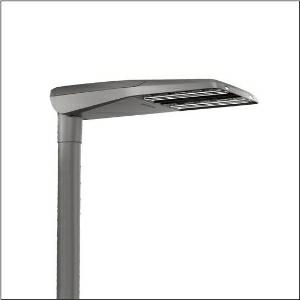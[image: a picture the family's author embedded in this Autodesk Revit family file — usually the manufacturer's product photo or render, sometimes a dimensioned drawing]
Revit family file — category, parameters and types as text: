
# Revit family: streetlight_sl_11_iq_midi___st1_0ab_5xc3n41f08le_a448
name_source: partatom
category: Lighting Fixtures
units: mm (PartAtom-declared; Revit-internal decimal feet)

## family parameters
Cut with Voids When Loaded = No
Host = Face
Light Source = No
Part Type = Normal
Room Calculation Point = No
Round Connector Dimension = Use Diameter
Shared = No

## types (1)
- --- (1 x LED, 8080 lm, 60.4 W, 4000K)
    Apparent Load = 60 VA
    CIE Flux Codes = 29 63 95 100 100
    Color Rendering = 70
    Color Temperature = 4000K
    Default Elevation = 1800 mm
    Description = Streetlight SL 11 iQ midi, mast luminaire, primary light control with 3 zone facetted reflector, of plastic, silver coated, highly specular, primary optical cover: cover, of PMMA, transparent, light distribution: ST1.0aB, light emission: direct distribution, primary light characteristic: asymmetric, installation type: post-top, side-entry, lamps: LED, High Power LED, rated values: 8.080lm | 60,4W | 133,8lm/W (begin service life); end service life: 8.080lm | 62,5W; at 50% lumin. flux: 4.040lm | 29,7W | 136lm/W, colour temperature: 4000K, colour rendering: CRI > 70, light colour: 740, light setting 1 begin service life: 100% | 8.080lm | 60,4W | 133,8lm/W | 4.000K, light setting 1 end service life: 62,5W, further light settings possible, control: optimised constant luminous flux control (CLO 2.0), Street-Remote, Desk-Remote (wireless, voltage-free reading and setting of iQ features in the workshop via application-optimized NFC function/RFID function), Light-Fading, Smart-Wire, Night-Set, Lumen-Switch, Temp-Guard, Auto-Match, with cable H07RN-F 3x 1.5mm², mains connection: 230..240V, AC, 50/60Hz, connection cable pre-assembled, cable length: 8,5m, luminaire housing, of diecast aluminium, powder-coated, SITECO metallic grey (DB 702S), please order mast flange separately, inclination adjustable without tools: 0°, 5°, 10°, 15° (post-top) | 0°, -5°, -10°, -15° (side-entry), sealing non-destructively replaceable, multi-level sealing system, length: 780mm, width: 376mm, height: 118mm, mast flange for spigot size: 42mm (side-entry): 5XC10008XM4, 60/48mm (side-entry/post-top): 5XC10108XM2, 76/60mm (side-entry/post-top): 5XC10108XM1, equipment: standard, protection rating (complete): IP66, insulation class (complete): insulation class II (safety insulation), certification: CE, ENEC, ENEC+, VDE, impact resistance: IK10, permissible operating ambient temperature for outdoor applications: -25..+50°C, standard-compliant lighting for roads and squares, Environmental Product Declaration (EPD) tested and certified by an independent institute, packaging unit: 1 piece

Light Distribution: ST1.0aB
    Height = 118 mm
    Lamp = 1 x LED
    Lamp Light Flux = 8080 lm
    Lamp Power = 60.4 W
    Lamp count = 1
    Length = 780 mm
    Luminous efficacy = 134 lm/W
    Manufacturer = Siteco
    ModVariant = No
    Model = 5XC3N41F08LE
    Number of Poles = 1
    OnlyDefault = Yes
    Power Factor = 1
    Product Name = Streetlight SL 11 iQ midi | ST1.0aB
    Product group = mast luminaire | pylon top
    ProductGroupID = 6100
    Protection Class = Protection class II
    Protection Degree = IP 66
    RLX_Detail_Level = 1
    RLX_Emergency_Light_Flux = 0 lm
    RLX_Emergency_Type = 0
    RLX_Emergency_Type_DB = No
    RlxData = <blob elided: 70221 chars, md5=709eb55e>
    Socket = socket
    Standby Power = 0 W
    System Light Flux = 8080 lm
    System Power = 60 W
    Type Comments = factory setting: luminous flux: 100 % | dim-lin: 254 | 520 mA
    Type Image = l_1005960.jpg
    URL = http://relux.com
    VarID = @adj_091895
    Voltage = 0 V
    Weight = 0.00 kg
    Width = 376 mm

## geometry (parser evidence)
native form markers: Blend x4, Sweep x12
no freeform markers — native parametric forms only
